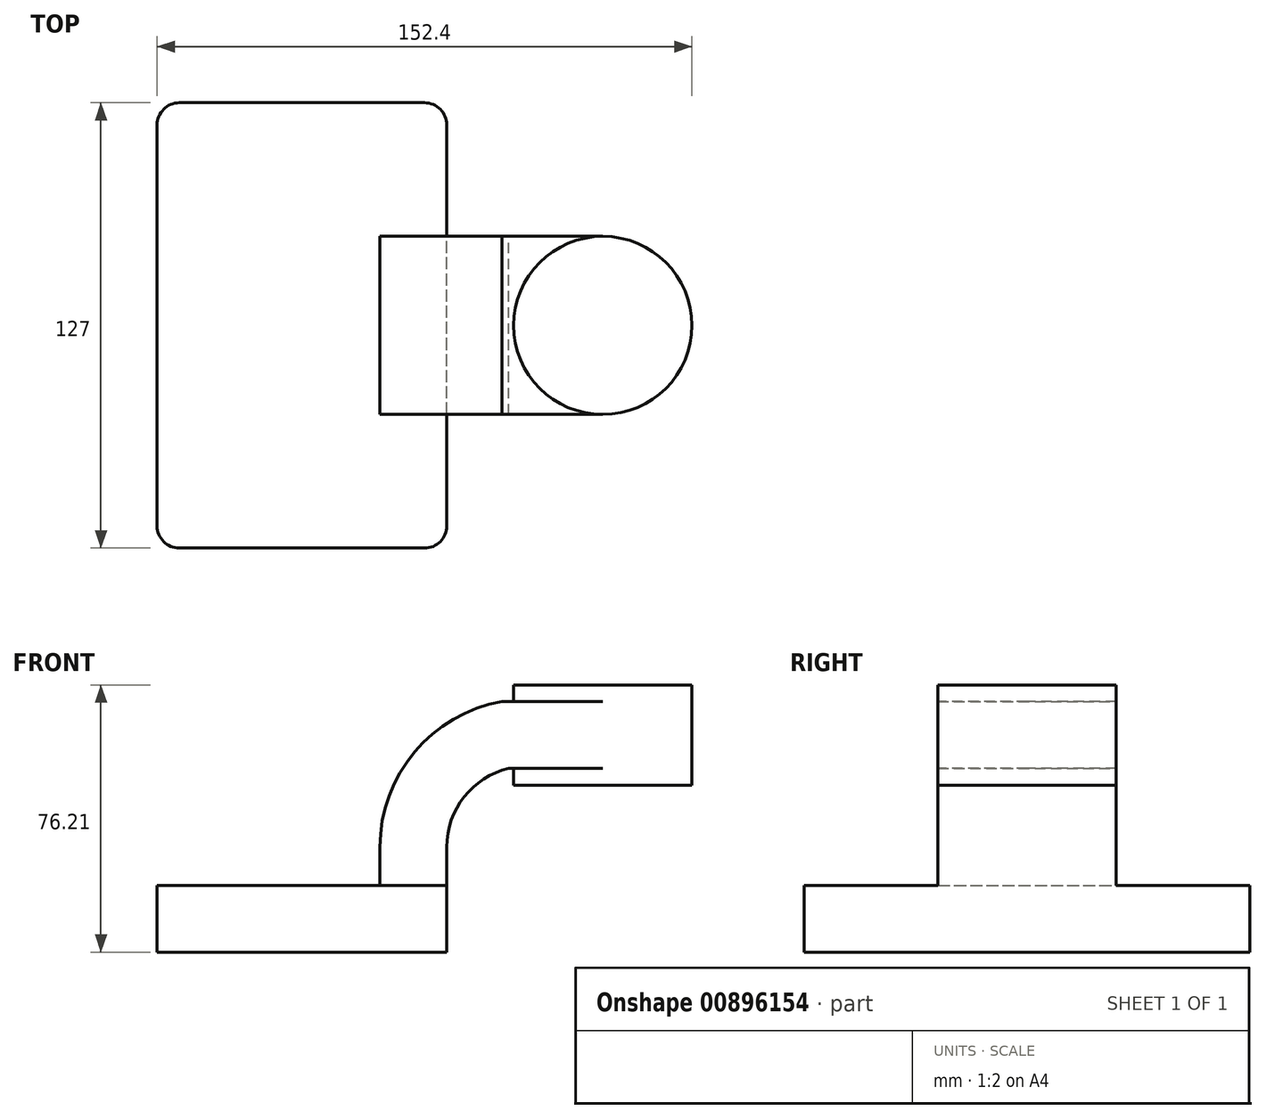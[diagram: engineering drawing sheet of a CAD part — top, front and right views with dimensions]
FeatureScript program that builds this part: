
annotation { "Feature Type Name" : "Feature", "Feature Type Description" : "" }
export const myFeature = defineFeature(function(context is Context, id is Id, definition is map)
    precondition{}
    {
        {
            var Q0;
            Q0=qCreatedBy(makeId("Front.planeOp"),FACE);
            var sketch = newSketch(context, id + "F0", { "sketchPlane" : qUnion([Q0])});
            skLineSegment(sketch, "E0.bottom", {"start": v(-41.28, 9.52) * mm, "end": v(41.28, 9.53) * mm});
            skLineSegment(sketch, "E0.top", {"start": v(-41.28, -9.53) * mm, "end": v(41.28, -9.53) * mm});
            skLineSegment(sketch, "E0.left", {"start": v(-41.28, 9.52) * mm, "end": v(-41.28, -9.53) * mm});
            skLineSegment(sketch, "E0.right", {"start": v(41.27, 9.53) * mm, "end": v(41.28, -9.52) * mm});
            skPoint(sketch, "E0.middle", {"position": v(0, 0) * mm});
            skLineSegment(sketch, "E1.bottom", {"start": v(111.12, 66.68) * mm, "end": v(60.32, 66.68) * mm});
            skLineSegment(sketch, "E1.top", {"start": v(111.12, 38.1) * mm, "end": v(60.32, 38.1) * mm});
            skLineSegment(sketch, "E1.left", {"start": v(111.12, 66.68) * mm, "end": v(111.12, 38.1) * mm});
            skLineSegment(sketch, "E1.right", {"start": v(60.32, 66.68) * mm, "end": v(60.32, 38.1) * mm});
            skPoint(sketch, "E1.middle", {"position": v(85.72, 52.39) * mm});
            skLineSegment(sketch, "E2", {"start": v(41.27, 9.53) * mm, "end": v(41.27, 20.42) * mm});
            skLineSegment(sketch, "E3", {"start": v(85.72, 15900.96) * mm, "end": v(15903.18, 15900.96) * mm});
            skArc(sketch, "E4", {"start": v(41.27, 20.42) * mm, "mid": v(46.23, 34.71) * mm, "end": v(58.96, 42.88) * mm});
            skLineSegment(sketch, "E5", {"start": v(58.96, 42.88) * mm, "end": v(99.97, 42.88) * mm});
            skLineSegment(sketch, "E6.0", {"start": v(57.04, 61.93) * mm, "end": v(99.97, 61.93) * mm});
            skArc(sketch, "E6.1", {"start": v(22.22, 20.42) * mm, "mid": v(32.08, 47.5) * mm, "end": v(57.04, 61.93) * mm});
            skLineSegment(sketch, "E6.2", {"start": v(22.22, 9.53) * mm, "end": v(22.22, 20.42) * mm});
            skLineSegment(sketch, "E7", {"start": v(85.72, 38.1) * mm, "end": v(85.72, 66.68) * mm});
            skFitSpline(sketch, "E8", {"points": [v(136.73, 151.84) * mm, v(125.1, 149.73) * mm], "startDerivative": vector(-11.62, -2.11) * mm, "endDerivative": vector(-11.62, -2.11) * mm});
            skFitSpline(sketch, "E9", {"points": [v(-41.28, 9.52) * mm, v(57.04, 61.93) * mm], "startDerivative": vector(6.2, 105.74) * mm, "endDerivative": vector(127.86, 2.32) * mm});
            skSolve(sketch);
        }
        {
            var Q0;
            Q0=makeQuery(id+"F0.imprint","IMPRINT",FACE,{"disambiguationData":[TD([[makeQuery(id+"F0.imprint","IMPRINT",EDGE,{"derivedFrom":sQuery(id+"F0.wireOp",EDGE,"E0.top")}),1.0]])]});
            extrude(context, id + "F1", {"entities" : qUnion([Q0]), "endBound" : BoundingType.SYMMETRIC, "depth" : 127 * mm, "offsetDistance" : 25.4 * mm});
        }
        {
            var Q0;
            {var subQ1=sQuery(id+"F0.wireOp",EDGE,"E2");Q0=makeQuery(id+"F0.imprint","IMPRINT",FACE,{"disambiguationData":[TD([[makeQuery(id+"F0.imprint","IMPRINT",EDGE,{"derivedFrom":subQ1}),1.0]])]});}
            var Q1;
            {var subQ0=sQuery(id+"F0.wireOp",EDGE,"E6.0");var subQ1=sQuery(id+"F0.wireOp",EDGE,"E1.right");var subQ2=makeQuery(id+"F0.imprint","INTERSECT",VERTEX,{"derivedFrom":[subQ1,subQ0]});Q1=makeQuery(id+"F0.imprint","IMPRINT",FACE,{"disambiguationData":[TD([[makeQuery(id+"F0.imprint","IMPRINT",EDGE,{"disambiguationData":[TD([[subQ2,-1.0]])],"derivedFrom":subQ1}),1.0]])]});}
            extrude(context, id + "F2", {"entities" : qUnion([Q0, Q1]), "operationType" : NewBodyOperationType.ADD, "endBound" : BoundingType.SYMMETRIC, "depth" : 50.8 * mm, "offsetDistance" : 25.4 * mm});
        }
        {
            var Q0;
            Q0=makeQuery(id+"F0.imprint","IMPRINT",FACE,{"disambiguationData":[TD([[makeQuery(id+"F0.imprint","IMPRINT",EDGE,{"derivedFrom":sQuery(id+"F0.wireOp",EDGE,"E6.1")}),1.0]])]});
            extrude(context, id + "F3", {"entities" : qUnion([Q0]), "operationType" : NewBodyOperationType.ADD, "endBound" : BoundingType.SYMMETRIC, "depth" : 15.88 * mm, "offsetDistance" : 25.4 * mm});
        }
        {
            var Q0;
            {var subQ4=sQuery(id+"F0.wireOp",EDGE,"E1.left");Q0=makeQuery(id+"F0.imprint","IMPRINT",FACE,{"disambiguationData":[TD([[makeQuery(id+"F0.imprint","IMPRINT",EDGE,{"derivedFrom":subQ4}),-1.0]])]});}
            var Q1;
            Q1=sQuery(id+"F0.wireOp",EDGE,"E7");
            revolve(context, id + "F4", {"operationType" : NewBodyOperationType.ADD, "surfaceOperationType" : NewSurfaceOperationType.NEW, "entities" : qUnion([Q0]), "axis" : qUnion([Q1]), "revolveType" : RevolveType.FULL});
        }
        {
            var Q0;
            Q0=makeQuery(id+"F1.opExtrude","CAP_EDGE",EDGE,{"disambiguationData":[OSD([sQuery(id+"F0.wireOp",EDGE,"E0.left")])],"isStart":false});
            var Q1;
            Q1=makeQuery(id+"F1.opExtrude","CAP_EDGE",EDGE,{"disambiguationData":[OSD([sQuery(id+"F0.wireOp",EDGE,"E0.right")])],"isStart":false});
            var Q2;
            Q2=makeQuery(id+"F1.opExtrude","CAP_EDGE",EDGE,{"disambiguationData":[OSD([sQuery(id+"F0.wireOp",EDGE,"E0.left")])],"isStart":true});
            var Q3;
            Q3=makeQuery(id+"F1.opExtrude","CAP_EDGE",EDGE,{"disambiguationData":[OSD([sQuery(id+"F0.wireOp",EDGE,"E0.right")])],"isStart":true});
            fillet(context, id + "F5", {"entities" : qUnion([Q0, Q1, Q2, Q3]), "radius" : 6.35 * mm, "tangentPropagation" : true, "allowEdgeOverflow" : false});
        }
    });
